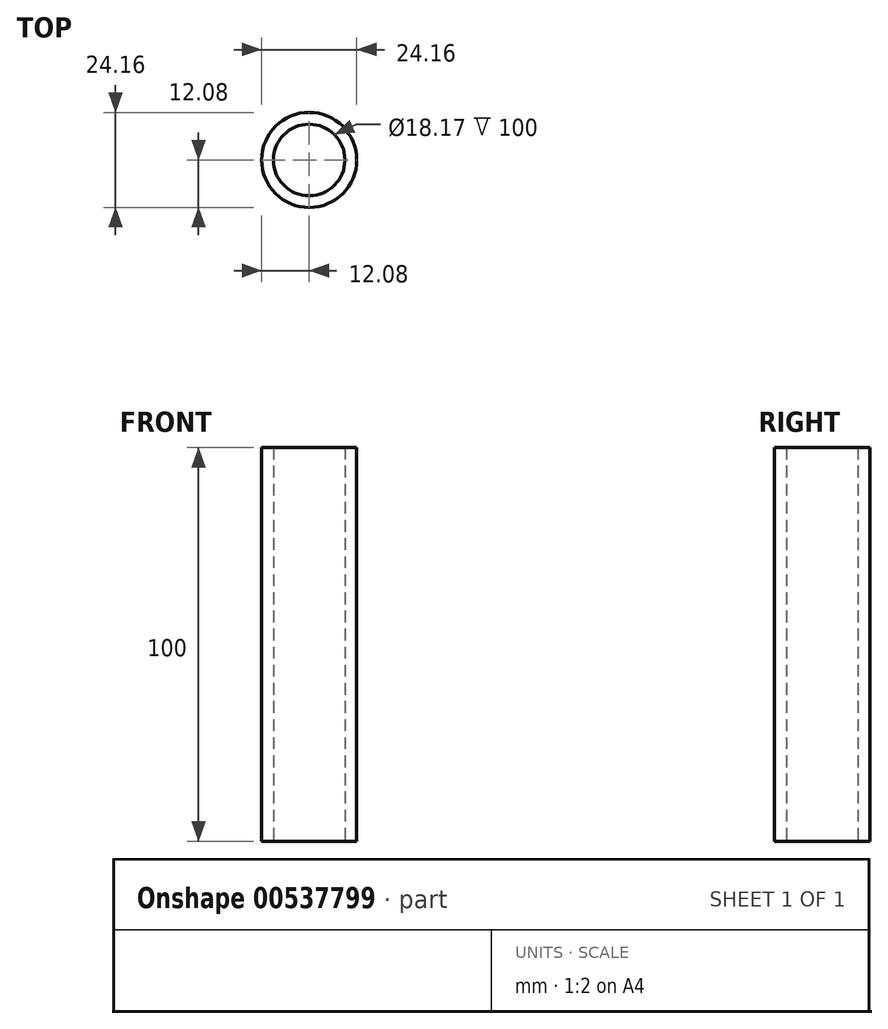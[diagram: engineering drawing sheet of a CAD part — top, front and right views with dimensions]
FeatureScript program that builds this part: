
annotation { "Feature Type Name" : "Feature", "Feature Type Description" : "" }
export const myFeature = defineFeature(function(context is Context, id is Id, definition is map)
    precondition{}
    {
        {
            var Q0;
            Q0=qCreatedBy(makeId("Top.planeOp"),FACE);
            var sketch = newSketch(context, id + "F0", { "sketchPlane" : qUnion([Q0])});
            skCircle(sketch, "E0", {"center": v(0, 0) * mm, "radius": 12.08 * mm});
            skCircle(sketch, "E1", {"center": v(0, 0) * mm, "radius": 9.08 * mm});
            skSolve(sketch);
        }
        {
            var Q0;
            Q0 = qSketchRegion(id + "F0", true);
            extrude(context, id + "F1", {"entities" : qUnion([Q0]), "depth" : 100 * mm, "offsetDistance" : 25 * mm});
        }
    });
